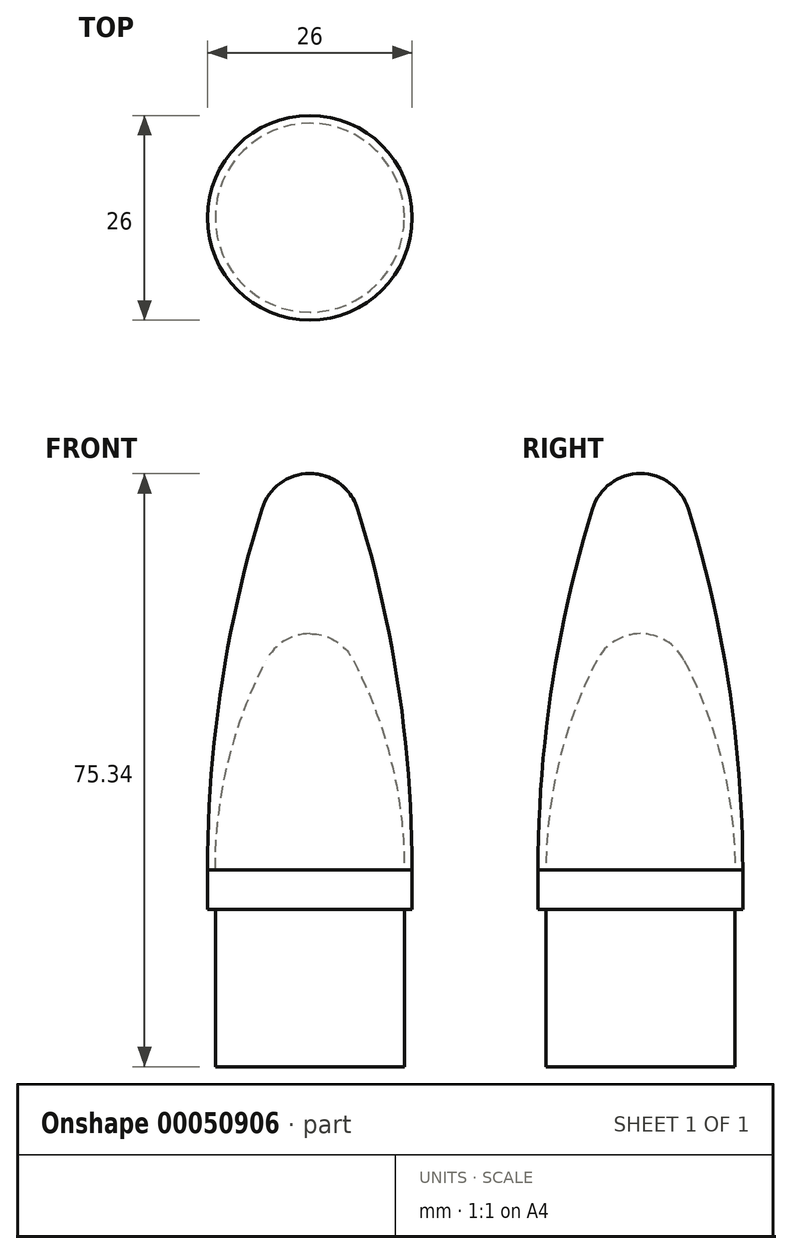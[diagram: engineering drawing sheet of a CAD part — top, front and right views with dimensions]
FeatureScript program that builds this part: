
annotation { "Feature Type Name" : "Feature", "Feature Type Description" : "" }
export const myFeature = defineFeature(function(context is Context, id is Id, definition is map)
    precondition{}
    {
        {
            var Q0;
            Q0=qCreatedBy(makeId("Front.planeOp"),FACE);
            var sketch = newSketch(context, id + "F0", { "sketchPlane" : qUnion([Q0])});
            skLineSegment(sketch, "E0", {"start": v(0, 0) * mm, "end": v(12, 0) * mm});
            skLineSegment(sketch, "E1", {"start": v(12, 0) * mm, "end": v(12, 20) * mm});
            skLineSegment(sketch, "E2", {"start": v(0, 0) * mm, "end": v(0, 55) * mm});
            skArc(sketch, "E3", {"start": v(5.53, 51.63) * mm, "mid": v(3.24, 54.1) * mm, "end": v(0, 55) * mm});
            skLineSegment(sketch, "E4", {"start": v(12, 20) * mm, "end": v(13, 20) * mm});
            skLineSegment(sketch, "E5", {"start": v(13, 20) * mm, "end": v(13, 25) * mm});
            skLineSegment(sketch, "E6", {"start": v(13, 25) * mm, "end": v(12, 25) * mm});
            skArc(sketch, "E7", {"start": v(12, 25) * mm, "mid": v(10.36, 38.7) * mm, "end": v(5.53, 51.63) * mm});
            skSolve(sketch);
        }
        {
            var Q0;
            Q0=makeQuery(id+"F0.imprint","IMPRINT",FACE,{"disambiguationData":[TD([[makeQuery(id+"F0.imprint","IMPRINT",EDGE,{"derivedFrom":sQuery(id+"F0.wireOp",EDGE,"E0")}),1.0]])]});
            var Q1;
            Q1=sQuery(id+"F0.wireOp",EDGE,"E2");
            revolve(context, id + "F1", {"entities" : qUnion([Q0]), "axis" : qUnion([Q1]), "revolveType" : RevolveType.FULL});
        }
        {
            var Q0;
            Q0=qCreatedBy(makeId("Front.planeOp"),FACE);
            var sketch = newSketch(context, id + "F2", { "sketchPlane" : qUnion([Q0])});
            skArc(sketch, "E8", {"start": v(12, 25) * mm, "mid": v(10.36, 38.7) * mm, "end": v(5.53, 51.63) * mm});
            skArc(sketch, "E9", {"start": v(5.53, 51.63) * mm, "mid": v(3.24, 54.1) * mm, "end": v(0, 55) * mm});
            skLineSegment(sketch, "E10", {"start": v(13, 25) * mm, "end": v(12, 25) * mm});
            skArc(sketch, "E11", {"start": v(13, 25) * mm, "mid": v(11.26, 48.2) * mm, "end": v(6.07, 70.87) * mm});
            skArc(sketch, "E12", {"start": v(6.07, 70.87) * mm, "mid": v(3.77, 74.1) * mm, "end": v(0, 75.34) * mm});
            skLineSegment(sketch, "E13.trimOffspring", {"start": v(0, 55) * mm, "end": v(0, 75.34) * mm});
            skPoint(sketch, "E14.orphan", {"position": v(-5.53, 51.63) * mm});
            skPoint(sketch, "E15.end.orphan", {"position": v(-12, 25) * mm});
            skPoint(sketch, "E16.end.orphan", {"position": v(-13, 25) * mm});
            skLineSegment(sketch, "E17", {"start": v(13, 25) * mm, "end": v(13, 83.7) * mm, "construction": true});
            skSolve(sketch);
        }
        {
            var Q0;
            Q0=makeQuery(id+"F2.imprint","IMPRINT",FACE,{"disambiguationData":[TD([[makeQuery(id+"F2.imprint","IMPRINT",EDGE,{"derivedFrom":sQuery(id+"F2.wireOp",EDGE,"E8")}),-1.0]])]});
            var Q1;
            Q1=sQuery(id+"F2.wireOp",EDGE,"E13.trimOffspring");
            revolve(context, id + "F3", {"entities" : qUnion([Q0]), "axis" : qUnion([Q1]), "revolveType" : RevolveType.FULL});
        }
    });
